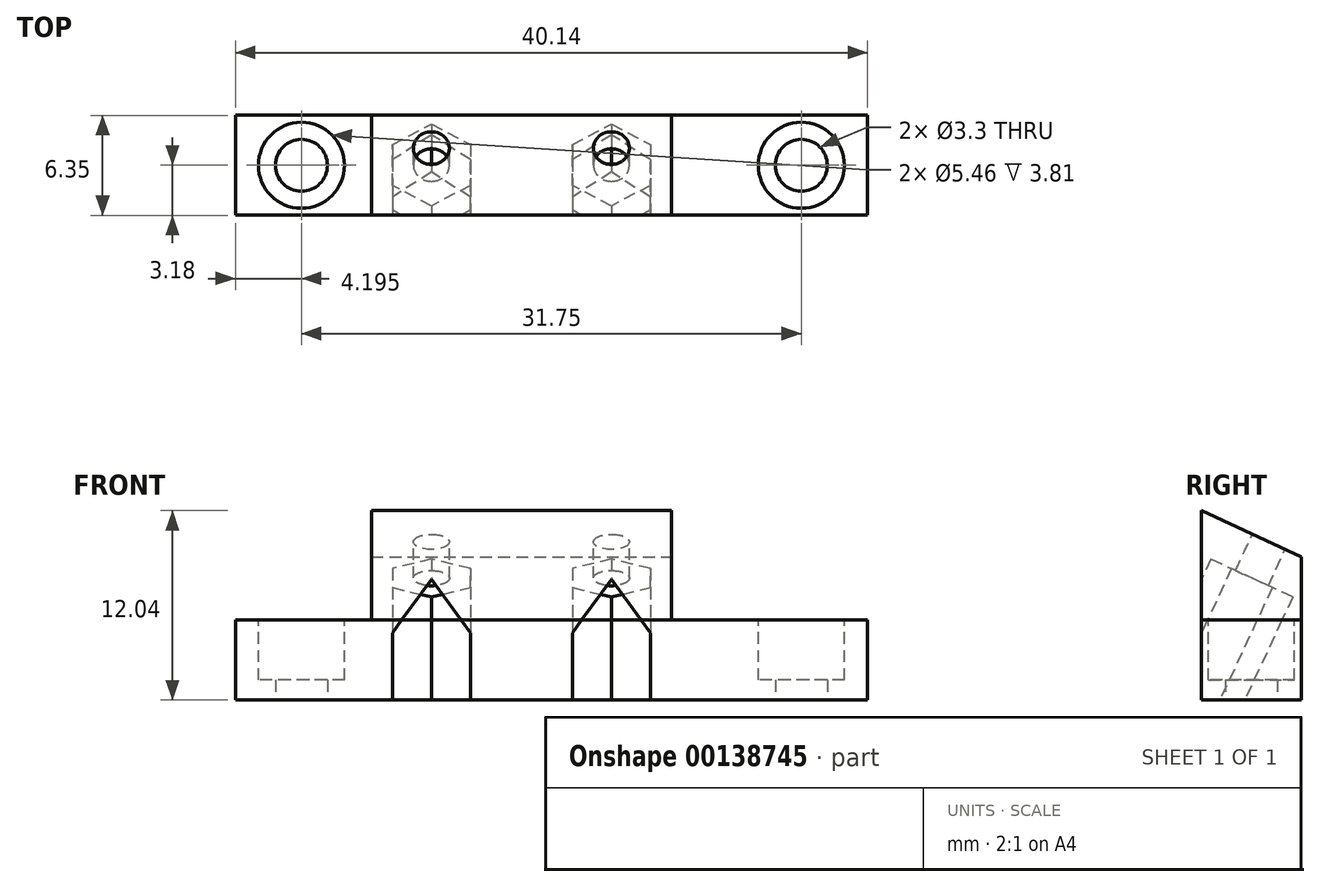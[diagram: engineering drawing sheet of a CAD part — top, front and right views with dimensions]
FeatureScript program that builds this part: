
annotation { "Feature Type Name" : "Feature", "Feature Type Description" : "" }
export const myFeature = defineFeature(function(context is Context, id is Id, definition is map)
    precondition{}
    {
        {
            var Q0;
            Q0=qCreatedBy(makeId("Top.planeOp"),FACE);
            var sketch = newSketch(context, id + "F0", { "sketchPlane" : qUnion([Q0])});
            skLineSegment(sketch, "E0.bottom", {"start": v(28.58, -3.18) * mm, "end": v(-28.58, -3.17) * mm});
            skLineSegment(sketch, "E0.top", {"start": v(22.23, 3.17) * mm, "end": v(-22.23, 3.17) * mm});
            skPoint(sketch, "E0.middle", {"position": v(0, 0) * mm});
            skCircle(sketch, "E1", {"center": v(15.88, 0) * mm, "radius": 1.65 * mm});
            skCircle(sketch, "E2", {"center": v(-15.88, 0) * mm, "radius": 1.65 * mm});
            skLineSegment(sketch, "E3.top", {"start": v(-28.58, 4.45) * mm, "end": v(-22.23, 4.45) * mm});
            skLineSegment(sketch, "E3.right", {"start": v(-22.23, 3.17) * mm, "end": v(-22.23, 4.45) * mm});
            skLineSegment(sketch, "E4.top", {"start": v(28.58, 4.45) * mm, "end": v(22.23, 4.45) * mm});
            skLineSegment(sketch, "E4.right", {"start": v(22.23, 3.18) * mm, "end": v(22.23, 4.45) * mm});
            skLineSegment(sketch, "E5", {"start": v(28.58, 4.45) * mm, "end": v(28.58, -3.17) * mm});
            skLineSegment(sketch, "E6", {"start": v(-28.58, 4.45) * mm, "end": v(-28.58, -3.18) * mm});
            skSolve(sketch);
        }
        {
            var Q0;
            Q0=qSketchRegion(id+"F0",true);
            extrude(context, id + "F1", {"entities" : qUnion([Q0]), "depth" : 5.08 * mm});
        }
        {
            var Q0;
            Q0=makeQuery(id+"F1.opExtrude","CAP_FACE",FACE,{"disambiguationData":[OSD([sQuery(id+"F0.wireOp",EDGE,"E0.bottom"),sQuery(id+"F0.wireOp",EDGE,"E0.top"),sQuery(id+"F0.wireOp",EDGE,"E1"),sQuery(id+"F0.wireOp",EDGE,"E2"),sQuery(id+"F0.wireOp",EDGE,"E3.top"),sQuery(id+"F0.wireOp",EDGE,"E3.right"),sQuery(id+"F0.wireOp",EDGE,"E4.top"),sQuery(id+"F0.wireOp",EDGE,"E4.right"),sQuery(id+"F0.wireOp",EDGE,"E5"),sQuery(id+"F0.wireOp",EDGE,"E6"),sQuery(id+"F0.wireOp",EDGE,"588c2650-f2db-4d57-a395-859ed4c48b6a"),sQuery(id+"F0.wireOp",EDGE,"e8d0fd80-d2a9-4f85-b5ed-e0f9fc0f3cee")])],"isStart":false});
            var sketch = newSketch(context, id + "F2", { "sketchPlane" : qUnion([Q0])});
            skCircle(sketch, "E7", {"center": v(-15.88, 0) * mm, "radius": 2.73 * mm});
            skCircle(sketch, "E8", {"center": v(15.88, 0) * mm, "radius": 2.73 * mm});
            skSolve(sketch);
        }
        {
            var Q0;
            Q0=qSketchRegion(id+"F2",true);
            extrude(context, id + "F3", {"entities" : qUnion([Q0]), "operationType" : NewBodyOperationType.REMOVE, "oppositeDirection" : true, "depth" : 3.8 * mm});
        }
        {
            var Q0;
            Q0=makeQuery(id+"F1.opExtrude","SWEPT_FACE",FACE,{"disambiguationData":[OSD([sQuery(id+"F0.wireOp",EDGE,"E5")])]});
            var sketch = newSketch(context, id + "F4", { "sketchPlane" : qUnion([Q0])});
            skLineSegment(sketch, "E9.bottom", {"start": v(-3.17, 5.08) * mm, "end": v(4.45, 5.08) * mm});
            skLineSegment(sketch, "E9.left", {"start": v(-3.17, 5.08) * mm, "end": v(-3.17, 12.04) * mm});
            skLineSegment(sketch, "E10", {"start": v(3.18, 9.08) * mm, "end": v(-3.17, 12.04) * mm});
            skLineSegment(sketch, "E11", {"start": v(3.18, 9.08) * mm, "end": v(3.18, 5.08) * mm});
            skSolve(sketch);
        }
        {
            var Q0;
            Q0=qSketchRegion(id+"F4",true);
            extrude(context, id + "F5", {"entities" : qUnion([Q0]), "oppositeDirection" : true, "depth" : 57.15 * mm});
        }
        {
            var Q0;
            Q0=makeQuery(id+"F5.opExtrude","SWEPT_FACE",FACE,{"disambiguationData":[OSD([sQuery(id+"F4.wireOp",EDGE,"E9.left")])]});
            var sketch = newSketch(context, id + "F6", { "sketchPlane" : qUnion([Q0])});
            skLineSegment(sketch, "E12.top", {"start": v(-28.58, 5.08) * mm, "end": v(28.58, 5.08) * mm});
            skLineSegment(sketch, "E13", {"start": v(-11.43, 12.04) * mm, "end": v(-11.43, 5.08) * mm});
            skLineSegment(sketch, "E14", {"start": v(7.62, 12.04) * mm, "end": v(7.62, 5.08) * mm});
            skLineSegment(sketch, "E15", {"start": v(-28.58, 5.08) * mm, "end": v(-28.58, 12.04) * mm});
            skLineSegment(sketch, "E16", {"start": v(28.58, 5.08) * mm, "end": v(28.58, 12.04) * mm});
            skLineSegment(sketch, "E17", {"start": v(-28.58, 12.04) * mm, "end": v(-11.43, 12.04) * mm});
            skLineSegment(sketch, "E18", {"start": v(7.62, 12.04) * mm, "end": v(28.58, 12.04) * mm});
            skSolve(sketch);
        }
        {
            var Q0;
            Q0=qSketchRegion(id+"F6",true);
            extrude(context, id + "F7", {"entities" : qUnion([Q0]), "operationType" : NewBodyOperationType.REMOVE, "endBound" : BoundingType.UP_TO_NEXT, "oppositeDirection" : true, "depth" : 25.4 * mm});
        }
        {
            var Q0;
            {var subQ0=sQuery(id+"F4.wireOp",EDGE,"E10");Q0=makeQuery(id+"F7.boolean.opBoolean","SPLIT",FACE,{"disambiguationData":[TD([makeQuery(id+"F7.opExtrude","SWEPT_FACE",FACE,{"disambiguationData":[OSD([sQuery(id+"F6.wireOp",EDGE,"E12.right")])]})])],"derivedFrom":makeQuery(id+"F5.opExtrude","SWEPT_FACE",FACE,{"disambiguationData":[OSD([subQ0])]})});}
            cPlane(context, id + "F8", {"entities" : qUnion([Q0]), "cplaneType" : CPlaneType.OFFSET, "offset" : 12.7 * mm, "oppositeDirection" : true, "width" : 152.4 * mm, "height" : 152.4 * mm});
        }
        {
            var Q0;
            Q0=makeQuery(id+"F1.opExtrude","SWEPT_FACE",FACE,{"disambiguationData":[OSD([sQuery(id+"F0.wireOp",EDGE,"E0.bottom")])]});
            var sketch = newSketch(context, id + "F9", { "sketchPlane" : qUnion([Q0])});
            skLineSegment(sketch, "E19.bottom", {"start": v(-28.58, 5.08) * mm, "end": v(-20.07, 5.08) * mm});
            skLineSegment(sketch, "E19.top", {"start": v(-28.58, 0) * mm, "end": v(-20.07, 0) * mm});
            skLineSegment(sketch, "E19.left", {"start": v(-28.58, 5.08) * mm, "end": v(-28.58, 0) * mm});
            skLineSegment(sketch, "E19.right", {"start": v(-20.07, 5.08) * mm, "end": v(-20.07, 0) * mm});
            skLineSegment(sketch, "E20.bottom", {"start": v(28.58, 5.08) * mm, "end": v(20.07, 5.08) * mm});
            skLineSegment(sketch, "E20.top", {"start": v(28.58, 0) * mm, "end": v(20.07, 0) * mm});
            skLineSegment(sketch, "E20.left", {"start": v(28.58, 5.08) * mm, "end": v(28.58, 0) * mm});
            skLineSegment(sketch, "E20.right", {"start": v(20.07, 5.08) * mm, "end": v(20.07, 0) * mm});
            skSolve(sketch);
        }
        {
            var Q0;
            Q0 = qSketchRegion(id + "F9", true);
            extrude(context, id + "F10", {"entities" : qUnion([Q0]), "operationType" : NewBodyOperationType.REMOVE, "endBound" : BoundingType.THROUGH_ALL, "oppositeDirection" : true, "depth" : 25.4 * mm});
        }
        {
            var Q0;
            Q0=makeQuery(id+"F5.opExtrude","SWEPT_FACE",FACE,{"disambiguationData":[OSD([sQuery(id+"F4.wireOp",EDGE,"E10")])]});
            var sketch = newSketch(context, id + "F11", { "sketchPlane" : qUnion([Q0])});
            skCircle(sketch, "E21", {"center": v(-7.62, -3.26) * mm, "radius": 1.14 * mm});
            skCircle(sketch, "E22", {"center": v(3.8, -3.26) * mm, "radius": 1.14 * mm});
            skSolve(sketch);
        }
        {
            var Q0;
            Q0 = qSketchRegion(id + "F11", true);
            extrude(context, id + "F12", {"entities" : qUnion([Q0]), "operationType" : NewBodyOperationType.REMOVE, "endBound" : BoundingType.THROUGH_ALL, "oppositeDirection" : true, "depth" : 25.4 * mm});
        }
        {
            var Q0;
            Q0=qCreatedBy(id+"F8.planeOp",FACE);
            var sketch = newSketch(context, id + "F13", { "sketchPlane" : qUnion([Q0])});
            skCircle(sketch, "E23.cCircle", {"center": v(-7.62, -3.26) * mm, "radius": 2.48 * mm, "construction": true});
            skLineSegment(sketch, "E23.0", {"start": v(-5.14, -1.83) * mm, "end": v(-5.14, -4.69) * mm});
            skLineSegment(sketch, "E23.1", {"start": v(-5.14, -4.69) * mm, "end": v(-7.62, -6.12) * mm});
            skLineSegment(sketch, "E23.2", {"start": v(-7.62, -6.12) * mm, "end": v(-10.1, -4.69) * mm});
            skLineSegment(sketch, "E23.3", {"start": v(-10.1, -4.69) * mm, "end": v(-10.1, -1.83) * mm});
            skLineSegment(sketch, "E23.4", {"start": v(-10.1, -1.83) * mm, "end": v(-7.62, -0.4) * mm});
            skLineSegment(sketch, "E23.5", {"start": v(-7.62, -0.4) * mm, "end": v(-5.14, -1.83) * mm});
            skPoint(sketch, "E23.0.midPoint", {"position": v(-5.14, -3.26) * mm});
            skCircle(sketch, "E24.cCircle", {"center": v(3.81, -3.26) * mm, "radius": 2.48 * mm, "construction": true});
            skLineSegment(sketch, "E24.0", {"start": v(3.8, -0.4) * mm, "end": v(6.29, -1.83) * mm});
            skLineSegment(sketch, "E24.1", {"start": v(6.29, -1.83) * mm, "end": v(6.29, -4.69) * mm});
            skLineSegment(sketch, "E24.2", {"start": v(6.29, -4.69) * mm, "end": v(3.81, -6.12) * mm});
            skLineSegment(sketch, "E24.3", {"start": v(3.81, -6.12) * mm, "end": v(1.33, -4.69) * mm});
            skLineSegment(sketch, "E24.4", {"start": v(1.33, -4.69) * mm, "end": v(1.33, -1.83) * mm});
            skLineSegment(sketch, "E24.5", {"start": v(1.33, -1.83) * mm, "end": v(3.8, -0.4) * mm});
            skPoint(sketch, "E24.0.midPoint", {"position": v(5.05, -1.11) * mm});
            skSolve(sketch);
        }
        {
            var Q0;
            Q0 = qSketchRegion(id + "F13", true);
            extrude(context, id + "F14", {"entities" : qUnion([Q0]), "operationType" : NewBodyOperationType.REMOVE, "depth" : 10.16 * mm});
        }
    });
